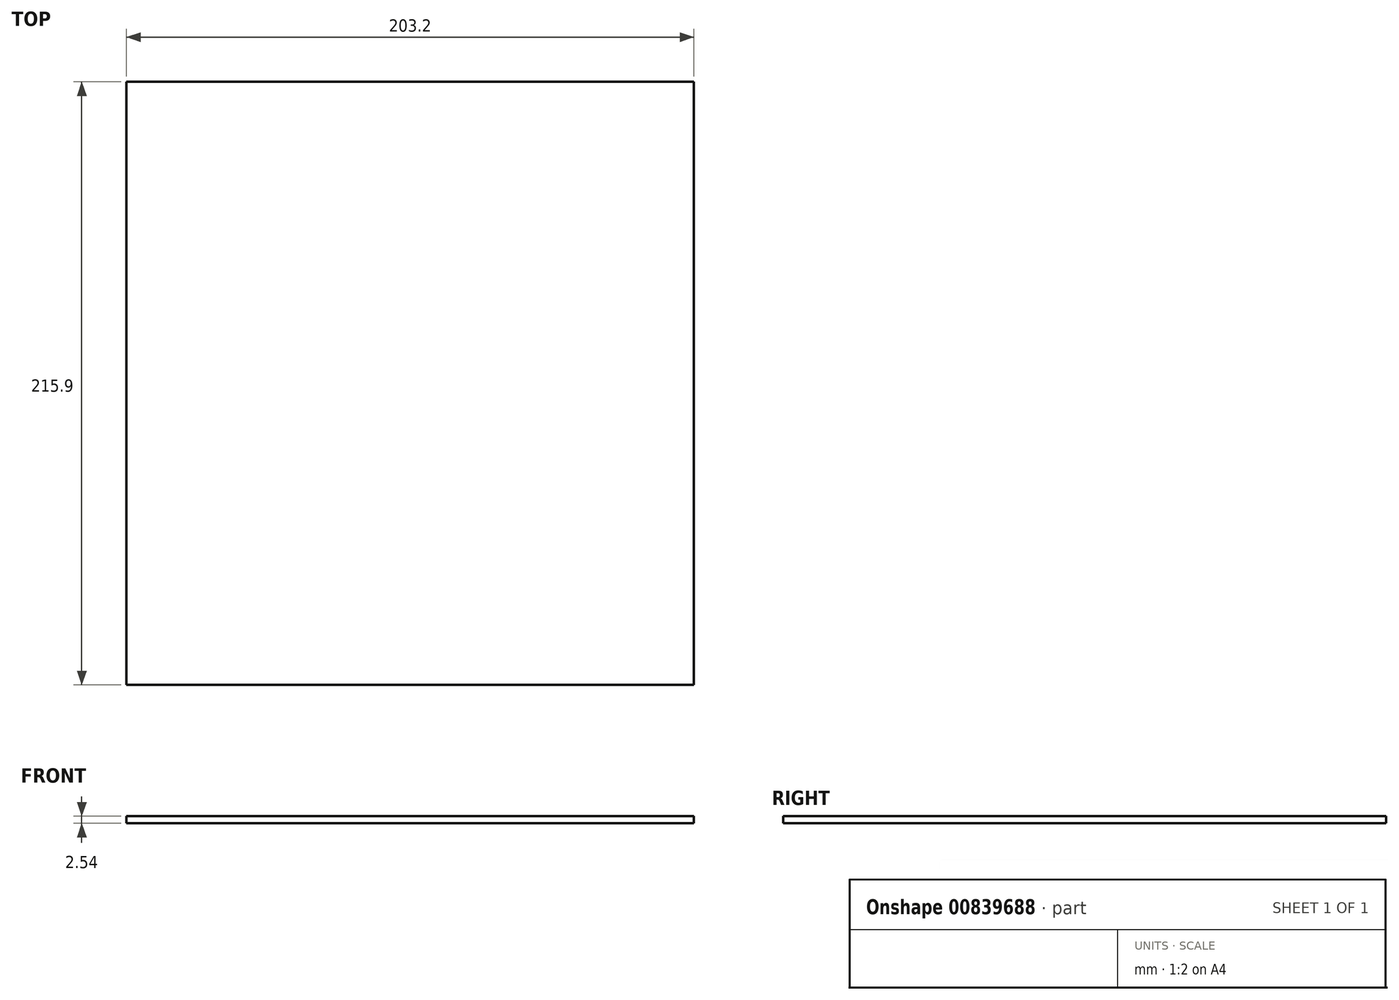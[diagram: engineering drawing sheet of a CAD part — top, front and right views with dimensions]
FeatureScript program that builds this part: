
annotation { "Feature Type Name" : "Feature", "Feature Type Description" : "" }
export const myFeature = defineFeature(function(context is Context, id is Id, definition is map)
    precondition{}
    {
        {
            var Q0;
            Q0=qCreatedBy(makeId("Top.planeOp"), FACE);
            var sketch = newSketch(context, id + "F0", { "sketchPlane" : qUnion([Q0])});
            skLineSegment(sketch, "E0.bottom", {"start": v(101.6, -107.95) * mm, "end": v(-101.6, -107.95) * mm});
            skLineSegment(sketch, "E0.top", {"start": v(101.6, 107.95) * mm, "end": v(-101.6, 107.95) * mm});
            skLineSegment(sketch, "E0.left", {"start": v(101.6, -107.95) * mm, "end": v(101.6, 107.95) * mm});
            skLineSegment(sketch, "E0.right", {"start": v(-101.6, -107.95) * mm, "end": v(-101.6, 107.95) * mm});
            skPoint(sketch, "E0.middle", {"position": v(0, 0) * mm});
            skSolve(sketch);
        }
        {
            var Q0;
            Q0 = qSketchRegion(id + "F0", true);
            extrude(context, id + "F1", {"entities" : qUnion([Q0]), "domain" : OperationDomain.MODEL, "flatOperationType" : FlatOperationType.REMOVE, "depth" : 2.54 * mm, "offsetDistance" : 25.4 * mm});
        }
    });
